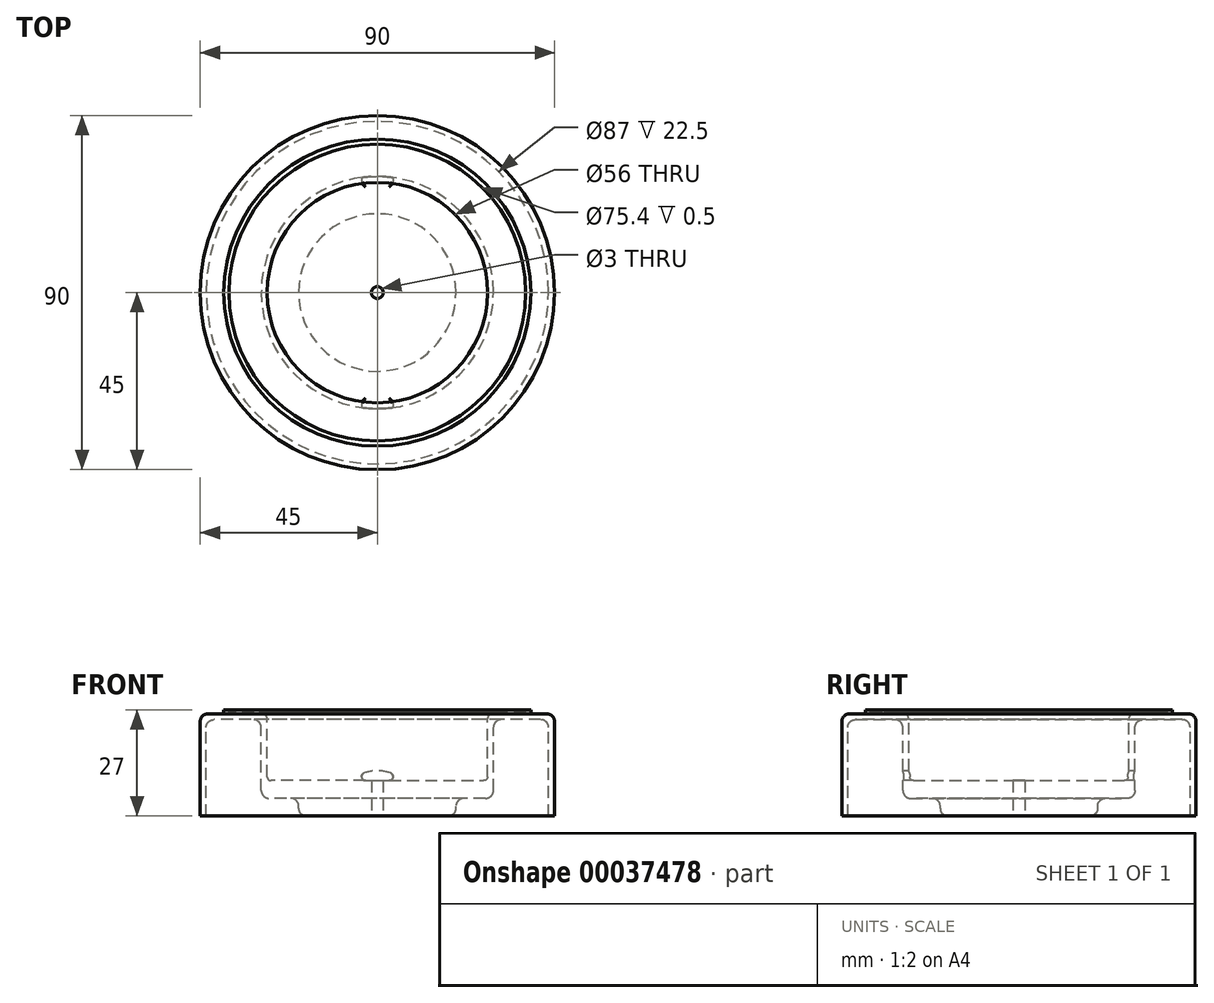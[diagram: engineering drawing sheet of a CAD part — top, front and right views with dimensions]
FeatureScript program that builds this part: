
annotation { "Feature Type Name" : "Feature", "Feature Type Description" : "" }
export const myFeature = defineFeature(function(context is Context, id is Id, definition is map)
    precondition{}
    {
        {
            var Q0;
            Q0=qCreatedBy(makeId("Right.planeOp"),FACE);
            var sketch = newSketch(context, id + "F0", { "sketchPlane" : qUnion([Q0])});
            skLineSegment(sketch, "E0", {"start": v(-45, 0) * mm, "end": v(-45, 24) * mm});
            skLineSegment(sketch, "E1", {"start": v(-43, 26) * mm, "end": v(-39, 26) * mm});
            skLineSegment(sketch, "E2", {"start": v(-39, 26) * mm, "end": v(-39, 27) * mm});
            skLineSegment(sketch, "E3", {"start": v(-39, 27) * mm, "end": v(-37.7, 27) * mm});
            skLineSegment(sketch, "E4", {"start": v(-37.7, 27) * mm, "end": v(-37.7, 26.5) * mm});
            skLineSegment(sketch, "E5", {"start": v(-37.7, 26.5) * mm, "end": v(-30, 26.5) * mm});
            skLineSegment(sketch, "E6", {"start": v(-28, 24.5) * mm, "end": v(-28, 10) * mm});
            skLineSegment(sketch, "E7", {"start": v(-27, 9) * mm, "end": v(0, 9) * mm});
            skLineSegment(sketch, "E8", {"start": v(-45, 0) * mm, "end": v(-43.5, 0) * mm});
            skLineSegment(sketch, "E9", {"start": v(-43.5, 0) * mm, "end": v(-43.5, 22.5) * mm});
            skLineSegment(sketch, "E10", {"start": v(-41.5, 24.5) * mm, "end": v(-31.5, 24.5) * mm});
            skLineSegment(sketch, "E11", {"start": v(-29.5, 22.5) * mm, "end": v(-29.5, 6.5) * mm});
            skLineSegment(sketch, "E12", {"start": v(-27.5, 4.5) * mm, "end": v(-22, 4.5) * mm});
            skLineSegment(sketch, "E13", {"start": v(-20, 2.5) * mm, "end": v(-20, 2) * mm});
            skLineSegment(sketch, "E14", {"start": v(0, 0) * mm, "end": v(-18, 0) * mm});
            skPoint(sketch, "E15.visualSharp", {"position": v(-43.5, 24.5) * mm});
            skArc(sketch, "E15.filletArc", {"start": v(-41.5, 24.5) * mm, "mid": v(-42.91, 23.91) * mm, "end": v(-43.5, 22.5) * mm});
            skPoint(sketch, "E16.visualSharp", {"position": v(-45, 26) * mm});
            skArc(sketch, "E16.filletArc", {"start": v(-43, 26) * mm, "mid": v(-44.41, 25.41) * mm, "end": v(-45, 24) * mm});
            skPoint(sketch, "E17.visualSharp", {"position": v(-29.5, 24.5) * mm});
            skArc(sketch, "E17.filletArc", {"start": v(-29.5, 22.5) * mm, "mid": v(-30.09, 23.91) * mm, "end": v(-31.5, 24.5) * mm});
            skPoint(sketch, "E18.visualSharp", {"position": v(-28, 26.5) * mm});
            skArc(sketch, "E18.filletArc", {"start": v(-28, 24.5) * mm, "mid": v(-28.59, 25.91) * mm, "end": v(-30, 26.5) * mm});
            skPoint(sketch, "E19.visualSharp", {"position": v(-29.5, 4.5) * mm});
            skArc(sketch, "E19.filletArc", {"start": v(-29.5, 6.5) * mm, "mid": v(-28.91, 5.09) * mm, "end": v(-27.5, 4.5) * mm});
            skPoint(sketch, "E20.visualSharp", {"position": v(-20, 0) * mm});
            skArc(sketch, "E20.filletArc", {"start": v(-20, 2) * mm, "mid": v(-19.41, 0.59) * mm, "end": v(-18, 0) * mm});
            skPoint(sketch, "E21.visualSharp", {"position": v(-20, 4.5) * mm});
            skArc(sketch, "E21.filletArc", {"start": v(-20, 2.5) * mm, "mid": v(-20.59, 3.91) * mm, "end": v(-22, 4.5) * mm});
            skPoint(sketch, "E22.visualSharp", {"position": v(-28, 9) * mm});
            skArc(sketch, "E22.filletArc", {"start": v(-28, 10) * mm, "mid": v(-27.7, 9.3) * mm, "end": v(-27, 9) * mm});
            skLineSegment(sketch, "E23", {"start": v(0, 9) * mm, "end": v(0, 0) * mm});
            skSolve(sketch);
        }
        {
            var Q0;
            Q0 = qSketchRegion(id + "F0", true);
            var Q1;
            Q1=sQuery(id+"F0.wireOp",EDGE,"E23");
            revolve(context, id + "F1", {"entities" : qUnion([Q0]), "axis" : qUnion([Q1]), "revolveType" : RevolveType.FULL});
        }
        {
            var Q0;
            Q0=qCreatedBy(makeId("Top.planeOp"),FACE);
            var sketch = newSketch(context, id + "F2", { "sketchPlane" : qUnion([Q0])});
            skCircle(sketch, "E24", {"center": v(0, 0) * mm, "radius": 1.5 * mm});
            skSolve(sketch);
        }
        {
            var Q0;
            Q0 = qSketchRegion(id + "F2", true);
            extrude(context, id + "F3", {"entities" : qUnion([Q0]), "operationType" : NewBodyOperationType.REMOVE, "depth" : 25 * mm});
        }
        {
            var Q0;
            Q0=qCreatedBy(makeId("Front.planeOp"),FACE);
            var sketch = newSketch(context, id + "F4", { "sketchPlane" : qUnion([Q0])});
            skLineSegment(sketch, "E25", {"start": v(3, 9) * mm, "end": v(0, 9) * mm});
            skArc(sketch, "E26", {"start": v(3, 9) * mm, "mid": v(3.99, 9.84) * mm, "end": v(3.32, 10.95) * mm});
            skLineSegment(sketch, "E27", {"start": v(0, 11) * mm, "end": v(0, 9) * mm, "construction": true});
            skLineSegment(sketch, "E28.MirrorCS", {"start": v(-3, 9) * mm, "end": v(0, 9) * mm});
            skArc(sketch, "E29.MirrorCS", {"start": v(-3, 9) * mm, "mid": v(-3.99, 9.84) * mm, "end": v(-3.32, 10.95) * mm});
            skArc(sketch, "E30", {"start": v(3.32, 10.95) * mm, "mid": v(0, 11.5) * mm, "end": v(-3.32, 10.95) * mm});
            skSolve(sketch);
        }
        {
            var Q0;
            Q0 = qSketchRegion(id + "F4", true);
            var Q1;
            Q1=makeQuery(id+"F1.opRevolve","SWEPT_FACE",FACE,{"disambiguationData":[OSD([sQuery(id+"F0.wireOp",EDGE,"E9")])]});
            var Q2;
            Q2=makeQuery(id+"F1.opRevolve","SWEPT_FACE",FACE,{"disambiguationData":[OSD([sQuery(id+"F0.wireOp",EDGE,"E9")])]});
            extrude(context, id + "F5", {"entities" : qUnion([Q0]), "operationType" : NewBodyOperationType.REMOVE, "endBound" : BoundingType.UP_TO_SURFACE, "oppositeDirection" : true, "endBoundEntityFace" : qUnion([Q1]), "depth" : 25 * mm, "hasSecondDirection" : true, "secondDirectionBound" : SecondDirectionBoundingType.UP_TO_SURFACE, "secondDirectionOppositeDirection" : false, "secondDirectionBoundEntityFace" : qUnion([Q2]), "secondDirectionDepth" : 25 * mm});
        }
    });
